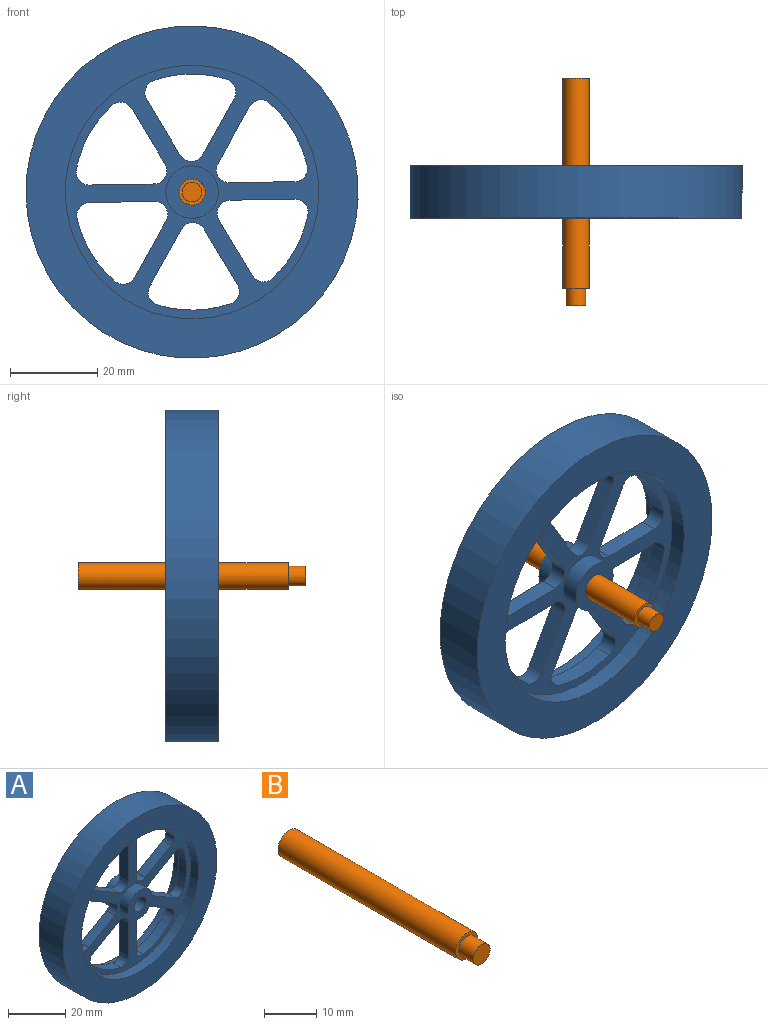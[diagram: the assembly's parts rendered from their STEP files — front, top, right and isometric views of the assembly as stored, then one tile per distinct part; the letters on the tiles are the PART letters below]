
ASSEMBLY  parts=2 mates=1
PART A: 48 faces, bbox 76x12x76 mm
  f0: plane 58x58mm, normal (0,1,0), area 915.2mm2, adj f4,f5,f12,f13,f14,f15,f16,f17
  f1: plane 58x58mm, normal (0,-1,0), area 915.2mm2, adj f9,f10,f12,f13,f14,f15,f16,f17
  f2: cylinder r=3mm len=12mm, axis (0,1,0), area 226.2mm2, adj f3,f11
  f3: plane 12x12mm, normal (0,1,0), area 84.8mm2, adj f2,f4
  f4: cylinder r=6mm len=12mm, axis (0,1,0), area 150.8mm2, adj f0,f3
  f5: cylinder r=29mm len=58mm, axis (0,1,0), area 728.8mm2, adj f0,f6
  f6: plane 76x76mm, normal (0,1,0), area 1894.4mm2, adj f5,f7
  f7: cylinder r=38mm len=76mm, axis (0,1,0), area 2865.1mm2, adj f6,f8
  f8: plane 76x76mm, normal (0,-1,0), area 1894.4mm2, adj f7,f9
  f9: cylinder r=29mm len=58mm, axis (0,1,0), area 728.8mm2, adj f1,f8
  f10: cylinder r=6mm len=12mm, axis (0,1,0), area 150.8mm2, adj f1,f11
  f11: plane 12x12mm, normal (0,-1,0), area 84.8mm2, adj f2,f10
  f12: plane 12.83x7.41mm, normal (-0.5,0,0.87), area 59.3mm2, adj f0,f1,f13,f17
  f13: cylinder r=3mm len=4.5mm, axis (0,1,0), area 25.1mm2, adj f0,f1,f12,f14
  f14: plane 14.81x4mm, normal (1,0,0), area 59.3mm2, adj f0,f1,f13,f15
  f15: cylinder r=3mm len=4mm, axis (0,1,0), area 21.4mm2, adj f0,f1,f14,f16
  f16: cylinder r=27mm len=14.43mm, axis (0,1,0), area 67.8mm2, adj f0,f1,f15,f17
  f17: cylinder r=3mm len=4.61mm, axis (0,1,0), area 21.4mm2, adj f0,f1,f12,f16
  f18: plane 14.81x4mm, normal (-1,0,0), area 59.3mm2, adj f0,f1,f19,f23
  f19: cylinder r=3mm len=4.5mm, axis (0,1,0), area 25.1mm2, adj f0,f1,f18,f20
  f20: plane 12.83x7.41mm, normal (0.5,0,0.87), area 59.3mm2, adj f0,f1,f19,f21
  f21: cylinder r=3mm len=4.61mm, axis (0,1,0), area 21.4mm2, adj f0,f1,f20,f22
  f22: cylinder r=27mm len=14.43mm, axis (0,1,0), area 67.8mm2, adj f0,f1,f21,f23
  f23: cylinder r=3mm len=4mm, axis (0,1,0), area 21.4mm2, adj f0,f1,f18,f22
  f24: plane 12.83x7.41mm, normal (0.5,0,-0.87), area 59.3mm2, adj f0,f1,f25,f29
  f25: cylinder r=3mm len=4.5mm, axis (0,1,0), area 25.1mm2, adj f0,f1,f24,f26
  f26: plane 14.81x4mm, normal (-1,0,0), area 59.3mm2, adj f0,f1,f25,f27
  f27: cylinder r=3mm len=4mm, axis (0,1,0), area 21.4mm2, adj f0,f1,f26,f28
  f28: cylinder r=27mm len=14.43mm, axis (0,1,0), area 67.8mm2, adj f0,f1,f27,f29
  f29: cylinder r=3mm len=4.61mm, axis (0,1,0), area 21.4mm2, adj f0,f1,f24,f28
  f30: plane 12.83x7.41mm, normal (-0.5,0,-0.87), area 59.3mm2, adj f0,f1,f31,f35
  f31: cylinder r=3mm len=5.2mm, axis (0,1,0), area 25.1mm2, adj f0,f1,f30,f32
  f32: plane 12.83x7.41mm, normal (-0.5,0,0.87), area 59.3mm2, adj f0,f1,f31,f33
  f33: cylinder r=3mm len=4.35mm, axis (0,1,0), area 21.4mm2, adj f0,f1,f32,f34
  f34: cylinder r=27mm len=16.66mm, axis (0,1,0), area 67.8mm2, adj f0,f1,f33,f35
  f35: cylinder r=3mm len=4.35mm, axis (0,1,0), area 21.4mm2, adj f0,f1,f30,f34
  f36: plane 12.83x7.41mm, normal (0.5,0,0.87), area 59.3mm2, adj f0,f1,f37,f41
  f37: cylinder r=3mm len=5.2mm, axis (0,1,0), area 25.1mm2, adj f0,f1,f36,f38
  f38: plane 12.83x7.41mm, normal (0.5,0,-0.87), area 59.3mm2, adj f0,f1,f37,f39
  f39: cylinder r=3mm len=4.35mm, axis (0,1,0), area 21.4mm2, adj f0,f1,f38,f40
  f40: cylinder r=27mm len=16.66mm, axis (0,1,0), area 67.8mm2, adj f0,f1,f39,f41
  f41: cylinder r=3mm len=4.35mm, axis (0,1,0), area 21.4mm2, adj f0,f1,f36,f40
  f42: plane 14.81x4mm, normal (1,0,0), area 59.3mm2, adj f0,f1,f43,f47
  f43: cylinder r=3mm len=4.5mm, axis (0,1,0), area 25.1mm2, adj f0,f1,f42,f44
  f44: plane 12.83x7.41mm, normal (-0.5,0,-0.87), area 59.3mm2, adj f0,f1,f43,f45
  f45: cylinder r=3mm len=4.61mm, axis (0,1,0), area 21.4mm2, adj f0,f1,f44,f46
  f46: cylinder r=27mm len=14.43mm, axis (0,1,0), area 67.8mm2, adj f0,f1,f45,f47
  f47: cylinder r=3mm len=4mm, axis (0,1,0), area 21.4mm2, adj f0,f1,f42,f46
PART B: 5 faces, bbox 6x52x6 mm
  f0: cylinder r=3mm len=48mm, axis (0,-1,0), area 904.8mm2, adj f1,f3
  f1: plane 6x6mm, normal (0,1,0), area 28.3mm2, adj f0
  f2: cylinder r=2.25mm len=4.5mm, axis (0,-1,0), area 56.5mm2, adj f3,f4
  f3: plane 6x6mm, normal (0,-1,0), area 12.4mm2, adj f0,f2
  f4: plane 4.5x4.5mm, normal (0,-1,0), area 15.9mm2, adj f2
PLACE A rot(axis=(0,-1,0),90.9deg) t=(124.35,0,-40.31)mm
PLACE B rot(axis=(0,-1,0),90.9deg) t=(124.35,0,-40.31)mm
MATE fastened B.f2 <-> A.f2  axis (0,-1,0) through (82,43,41)mm
